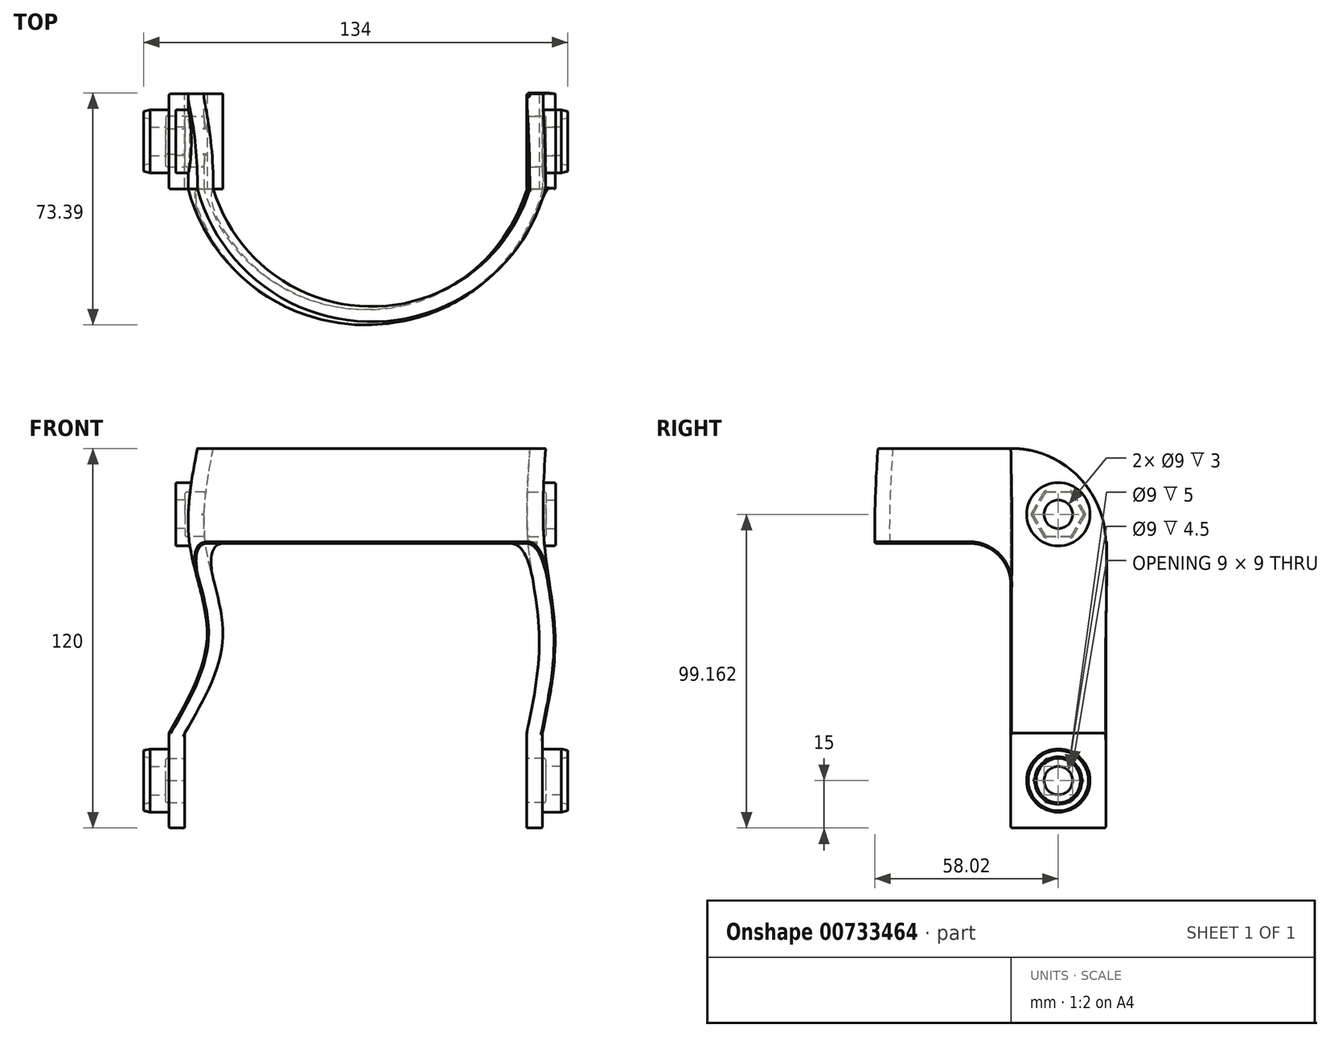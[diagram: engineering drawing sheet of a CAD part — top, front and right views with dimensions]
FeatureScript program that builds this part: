
annotation { "Feature Type Name" : "Feature", "Feature Type Description" : "" }
export const myFeature = defineFeature(function(context is Context, id is Id, definition is map)
    precondition{}
    {
        {
            var Q0;
            Q0=qCreatedBy(makeId("Top.planeOp"),FACE);
            cPlane(context, id + "F0", {"entities" : qUnion([Q0]), "cplaneType" : CPlaneType.OFFSET, "offset" : 30 * mm, "width" : 150 * mm, "height" : 150 * mm});
        }
        {
            var Q0;
            Q0=qCreatedBy(id+"F0.planeOp",FACE);
            var sketch = newSketch(context, id + "F1", { "sketchPlane" : qUnion([Q0])});
            skLineSegment(sketch, "E0", {"start": v(-54, 0) * mm, "end": v(-54, 15) * mm});
            skLineSegment(sketch, "E1", {"start": v(-54, 15) * mm, "end": v(-59, 15) * mm});
            skLineSegment(sketch, "E2", {"start": v(-59, 15) * mm, "end": v(-59, -15) * mm});
            skLineSegment(sketch, "E3", {"start": v(-54, -15) * mm, "end": v(-54, 0) * mm});
            skLineSegment(sketch, "E4", {"start": v(54, 0) * mm, "end": v(54, 15) * mm});
            skLineSegment(sketch, "E5", {"start": v(54, 15) * mm, "end": v(59, 15) * mm});
            skLineSegment(sketch, "E6", {"start": v(59, 15) * mm, "end": v(59, -15) * mm});
            skLineSegment(sketch, "E7", {"start": v(54, -15) * mm, "end": v(54, 0) * mm});
            skArc(sketch, "E8", {"start": v(-54, -15) * mm, "mid": v(0, -56.04) * mm, "end": v(54, -15) * mm});
            skArc(sketch, "E9", {"start": v(59, -15) * mm, "mid": v(0, -60.88) * mm, "end": v(-59, -15) * mm});
            skPoint(sketch, "E10", {"position": v(0, -56.04) * mm});
            skPoint(sketch, "E11", {"position": v(0, -60.88) * mm});
            skSolve(sketch);
        }
        {
            var Q0;
            Q0=qCreatedBy(makeId("Top.planeOp"),FACE);
            var sketch = newSketch(context, id + "F2", { "sketchPlane" : qUnion([Q0])});
            skLineSegment(sketch, "E12", {"start": v(-54, 0) * mm, "end": v(-54, 15) * mm});
            skLineSegment(sketch, "E13", {"start": v(-54, 15) * mm, "end": v(-59, 15) * mm});
            skLineSegment(sketch, "E14", {"start": v(-59, 15) * mm, "end": v(-59, -15) * mm});
            skLineSegment(sketch, "E15", {"start": v(-54, -15) * mm, "end": v(-54, 0) * mm});
            skLineSegment(sketch, "E16", {"start": v(54, 0) * mm, "end": v(54, 15) * mm});
            skLineSegment(sketch, "E17", {"start": v(54, 15) * mm, "end": v(59, 15) * mm});
            skLineSegment(sketch, "E18", {"start": v(59, 15) * mm, "end": v(59, -15) * mm});
            skLineSegment(sketch, "E19", {"start": v(54, -15) * mm, "end": v(54, 0) * mm});
            skArc(sketch, "E20", {"start": v(-54, -15) * mm, "mid": v(0, -56.04) * mm, "end": v(54, -15) * mm});
            skArc(sketch, "E21", {"start": v(59, -15) * mm, "mid": v(0, -60.88) * mm, "end": v(-59, -15) * mm});
            skPoint(sketch, "E22", {"position": v(0, -56.04) * mm});
            skPoint(sketch, "E23", {"position": v(0, -60.88) * mm});
            skSolve(sketch);
        }
        {
            var Q0;
            Q0=qCreatedBy(makeId("Top.planeOp"),FACE);
            cPlane(context, id + "F3", {"entities" : qUnion([Q0]), "cplaneType" : CPlaneType.OFFSET, "offset" : 60 * mm, "width" : 150 * mm, "height" : 150 * mm});
        }
        {
            var Q0;
            Q0=qCreatedBy(id+"F3.planeOp",FACE);
            var sketch = newSketch(context, id + "F4", { "sketchPlane" : qUnion([Q0])});
            skPoint(sketch, "E24", {"position": v(8, 0) * mm});
            skPoint(sketch, "E25", {"position": v(-42, 0) * mm});
            skPoint(sketch, "E26", {"position": v(58, 0) * mm});
            skLineSegment(sketch, "E27", {"start": v(-42, 0) * mm, "end": v(-42, -15) * mm});
            skLineSegment(sketch, "E28", {"start": v(-47, -15) * mm, "end": v(-47, 15) * mm});
            skLineSegment(sketch, "E29", {"start": v(-47, 15) * mm, "end": v(-42, 15) * mm});
            skLineSegment(sketch, "E30", {"start": v(-42, 15) * mm, "end": v(-42, 0) * mm});
            skLineSegment(sketch, "E31", {"start": v(58, 0) * mm, "end": v(58, 15) * mm});
            skLineSegment(sketch, "E32", {"start": v(58, 15) * mm, "end": v(63, 15) * mm});
            skLineSegment(sketch, "E33", {"start": v(63, 15) * mm, "end": v(63, -15) * mm});
            skLineSegment(sketch, "E34", {"start": v(58, -15) * mm, "end": v(58, 0) * mm});
            skArc(sketch, "E35", {"start": v(-42, -15) * mm, "mid": v(8, -52.2) * mm, "end": v(58, -15) * mm});
            skArc(sketch, "E36", {"start": v(-47, -15) * mm, "mid": v(8, -57) * mm, "end": v(63, -15) * mm});
            skSolve(sketch);
        }
        {
            var Q0;
            Q0=qCreatedBy(makeId("Top.planeOp"),FACE);
            cPlane(context, id + "F5", {"entities" : qUnion([Q0]), "cplaneType" : CPlaneType.OFFSET, "offset" : 90 * mm, "width" : 150 * mm, "height" : 150 * mm});
        }
        {
            var Q0;
            Q0=qCreatedBy(id+"F5.planeOp",FACE);
            var sketch = newSketch(context, id + "F6", { "sketchPlane" : qUnion([Q0])});
            skPoint(sketch, "E37", {"position": v(3.5, 0) * mm});
            skPoint(sketch, "E38", {"position": v(-47.5, 0) * mm});
            skPoint(sketch, "E39", {"position": v(54.5, 0) * mm});
            skLineSegment(sketch, "E40", {"start": v(-47.5, 0) * mm, "end": v(-47.5, 15) * mm});
            skLineSegment(sketch, "E41", {"start": v(-47.5, 15) * mm, "end": v(-52.5, 15) * mm});
            skLineSegment(sketch, "E42", {"start": v(-52.5, 15) * mm, "end": v(-52.5, -15) * mm});
            skLineSegment(sketch, "E43", {"start": v(-47.5, -15) * mm, "end": v(-47.5, 0) * mm});
            skLineSegment(sketch, "E44", {"start": v(54.5, 0) * mm, "end": v(54.5, 15.37) * mm});
            skLineSegment(sketch, "E45", {"start": v(54.5, 15.37) * mm, "end": v(59.6, 15.37) * mm});
            skLineSegment(sketch, "E46", {"start": v(59.6, 15.37) * mm, "end": v(59.6, -14.63) * mm});
            skLineSegment(sketch, "E47", {"start": v(54.5, -15) * mm, "end": v(54.5, 0) * mm});
            skArc(sketch, "E48", {"start": v(-47.5, -15) * mm, "mid": v(3.5, -53.16) * mm, "end": v(54.5, -15) * mm});
            skArc(sketch, "E49", {"start": v(-52.5, -15) * mm, "mid": v(3.69, -57.97) * mm, "end": v(59.6, -14.63) * mm});
            skSolve(sketch);
        }
        {
            var Q0;
            Q0=qCreatedBy(makeId("Top.planeOp"),FACE);
            cPlane(context, id + "F7", {"entities" : qUnion([Q0]), "cplaneType" : CPlaneType.OFFSET, "offset" : 120 * mm, "width" : 150 * mm, "height" : 150 * mm});
        }
        {
            var Q0;
            Q0=qCreatedBy(id+"F7.planeOp",FACE);
            var sketch = newSketch(context, id + "F8", { "sketchPlane" : qUnion([Q0])});
            skPoint(sketch, "E50", {"position": v(5, 0) * mm});
            skPoint(sketch, "E51", {"position": v(-45, 0) * mm});
            skPoint(sketch, "E52", {"position": v(55, 0) * mm});
            skLineSegment(sketch, "E53", {"start": v(-45, 0) * mm, "end": v(-45, 15) * mm});
            skLineSegment(sketch, "E54", {"start": v(-45, 15) * mm, "end": v(-50, 15) * mm});
            skLineSegment(sketch, "E55", {"start": v(-50, 15) * mm, "end": v(-50, -15) * mm});
            skLineSegment(sketch, "E56", {"start": v(-45, -15) * mm, "end": v(-45, 0) * mm});
            skLineSegment(sketch, "E57", {"start": v(55, 0) * mm, "end": v(55, -15) * mm});
            skLineSegment(sketch, "E58", {"start": v(60, -15) * mm, "end": v(60, 15) * mm});
            skLineSegment(sketch, "E59", {"start": v(60, 15) * mm, "end": v(55, 15) * mm});
            skLineSegment(sketch, "E60", {"start": v(55, 15) * mm, "end": v(55, 0) * mm});
            skArc(sketch, "E61", {"start": v(-45, -15) * mm, "mid": v(5, -52.2) * mm, "end": v(55, -15) * mm});
            skArc(sketch, "E62", {"start": v(-50, -15) * mm, "mid": v(5, -57) * mm, "end": v(60, -15) * mm});
            skSolve(sketch);
        }
        {
            var Q0;
            Q0=makeQuery(id+"F1.imprint","IMPRINT",FACE,{"disambiguationData":[TD([[makeQuery(id+"F1.imprint","IMPRINT",EDGE,{"derivedFrom":sQuery(id+"F1.wireOp",EDGE,"E0")}),1.0]])]});
            var Q1;
            Q1=makeQuery(id+"F4.imprint","IMPRINT",FACE,{"disambiguationData":[TD([[makeQuery(id+"F4.imprint","IMPRINT",EDGE,{"derivedFrom":sQuery(id+"F4.wireOp",EDGE,"E27")}),-1.0]])]});
            var Q2;
            Q2=makeQuery(id+"F6.imprint","IMPRINT",FACE,{"disambiguationData":[TD([[makeQuery(id+"F6.imprint","IMPRINT",EDGE,{"derivedFrom":sQuery(id+"F6.wireOp",EDGE,"E40")}),1.0]])]});
            var Q3;
            Q3=makeQuery(id+"F8.imprint","IMPRINT",FACE,{"disambiguationData":[TD([[makeQuery(id+"F8.imprint","IMPRINT",EDGE,{"derivedFrom":sQuery(id+"F8.wireOp",EDGE,"E53")}),1.0]])]});
            loft(context, id + "F9", {"sheetProfilesArray" : [{ "sheetProfileEntities" : qUnion([Q0]) }, { "sheetProfileEntities" : qUnion([Q1]) }, { "sheetProfileEntities" : qUnion([Q2]) }, { "sheetProfileEntities" : qUnion([Q3]) }]});
        }
        {
            var Q0;
            Q0=makeQuery(id+"F2.imprint","IMPRINT",FACE,{"disambiguationData":[TD([[makeQuery(id+"F2.imprint","IMPRINT",EDGE,{"derivedFrom":sQuery(id+"F2.wireOp",EDGE,"E12")}),1.0]])]});
            extrude(context, id + "F10", {"entities" : qUnion([Q0]), "operationType" : NewBodyOperationType.ADD, "depth" : 30 * mm, "offsetDistance" : 25 * mm});
        }
        {
            var Q0;
            Q0=qCreatedBy(makeId("Right.planeOp"),FACE);
            var sketch = newSketch(context, id + "F11", { "sketchPlane" : qUnion([Q0])});
            skPoint(sketch, "E63", {"position": v(82.65, 59.89) * mm});
            skPoint(sketch, "E64", {"position": v(-15, 120) * mm});
            skPoint(sketch, "E65", {"position": v(-15, 90) * mm});
            skArc(sketch, "E66", {"start": v(-15, 120) * mm, "mid": v(6.21, 111.21) * mm, "end": v(15, 90) * mm});
            skPoint(sketch, "E67", {"position": v(-28.01, 76.99) * mm});
            skArc(sketch, "E68", {"start": v(-15, 76.99) * mm, "mid": v(-18.81, 86.19) * mm, "end": v(-28.01, 90) * mm});
            skLineSegment(sketch, "E69", {"start": v(-15, 76.99) * mm, "end": v(-15, -61.51) * mm});
            skLineSegment(sketch, "E70", {"start": v(-15, -61.51) * mm, "end": v(-141.22, -61.51) * mm});
            skLineSegment(sketch, "E71", {"start": v(-141.22, -61.51) * mm, "end": v(-141.22, 174.74) * mm});
            skLineSegment(sketch, "E72", {"start": v(-141.22, 174.74) * mm, "end": v(85.32, 174.74) * mm});
            skLineSegment(sketch, "E73", {"start": v(85.32, 174.74) * mm, "end": v(15, 90) * mm});
            skLineSegment(sketch, "E74", {"start": v(-28.01, 90) * mm, "end": v(-81.35, 90) * mm});
            skLineSegment(sketch, "E75", {"start": v(-81.35, 90) * mm, "end": v(-81.35, 120) * mm});
            skLineSegment(sketch, "E76", {"start": v(-81.35, 120) * mm, "end": v(-15, 120) * mm});
            skSolve(sketch);
        }
        {
            var Q0;
            Q0=qSketchRegion(id+"F11",true);
            extrude(context, id + "F12", {"entities" : qUnion([Q0]), "operationType" : NewBodyOperationType.REMOVE, "oppositeDirection" : true, "depth" : 100 * mm, "offsetDistance" : 25 * mm, "hasSecondDirection" : true, "secondDirectionOppositeDirection" : false, "secondDirectionDepth" : 100 * mm});
        }
        {
            var Q0;
            Q0=makeQuery(id+"F10.opExtrude","SWEPT_FACE",FACE,{"disambiguationData":[OSD([sQuery(id+"F2.wireOp",EDGE,"E14")])]});
            var sketch = newSketch(context, id + "F13", { "sketchPlane" : qUnion([Q0])});
            skPoint(sketch, "E77", {"position": v(0, 15) * mm});
            skCircle(sketch, "E78", {"center": v(0, 15) * mm, "radius": 10 * mm});
            skSolve(sketch);
        }
        {
            var Q0;
            Q0=makeQuery(id+"F13.imprint","IMPRINT",FACE,{"disambiguationData":[TD([[makeQuery(id+"F13.imprint","IMPRINT",EDGE,{"derivedFrom":sQuery(id+"F13.wireOp",EDGE,"E78")}),1.0]])]});
            extrude(context, id + "F14", {"entities" : qUnion([Q0]), "operationType" : NewBodyOperationType.ADD, "depth" : 6 * mm, "offsetDistance" : 25 * mm});
        }
        {
            var Q0;
            Q0=qCreatedBy(makeId("Front.planeOp"),FACE);
            var sketch = newSketch(context, id + "F15", { "sketchPlane" : qUnion([Q0])});
            skPoint(sketch, "E79", {"position": v(-54, 15) * mm});
            skPoint(sketch, "E80", {"position": v(-49.01, 23.39) * mm});
            skPoint(sketch, "E81", {"position": v(-65, 15) * mm});
            skLineSegment(sketch, "E82", {"start": v(-65, 22) * mm, "end": v(-65, 25) * mm});
            skLineSegment(sketch, "E83", {"start": v(-65, 25) * mm, "end": v(-67, 24.5) * mm});
            skLineSegment(sketch, "E84", {"start": v(-67, 24.5) * mm, "end": v(-67, 22.5) * mm});
            skLineSegment(sketch, "E85", {"start": v(-67, 22.5) * mm, "end": v(-65, 22) * mm});
            skPoint(sketch, "E86", {"position": v(-65, 23.5) * mm});
            skPoint(sketch, "E87", {"position": v(-67, 23.5) * mm});
            skLineSegment(sketch, "E88", {"start": v(-65, 15) * mm, "end": v(-67, 15) * mm});
            skLineSegment(sketch, "E89", {"start": v(-65, 22) * mm, "end": v(-67, 22.5) * mm});
            skLineSegment(sketch, "E90", {"start": v(-67, 22.5) * mm, "end": v(-67, 24.5) * mm});
            skLineSegment(sketch, "E91", {"start": v(-67, 24.5) * mm, "end": v(-65, 25) * mm});
            skLineSegment(sketch, "E92", {"start": v(-65, 25) * mm, "end": v(-65, 22) * mm});
            skSolve(sketch);
        }
        {
            var Q0;
            Q0 = qSketchRegion(id + "F15", true);
            var Q1;
            Q1=sQuery(id+"F15.wireOp",EDGE,"E88");
            revolve(context, id + "F16", {"operationType" : NewBodyOperationType.ADD, "surfaceOperationType" : NewSurfaceOperationType.NEW, "entities" : qUnion([Q0]), "axis" : qUnion([Q1]), "revolveType" : RevolveType.FULL});
        }
        {
            var Q0;
            Q0=makeQuery(id+"F10.opExtrude","SWEPT_FACE",FACE,{"disambiguationData":[OSD([sQuery(id+"F2.wireOp",EDGE,"E12"),sQuery(id+"F2.wireOp",EDGE,"E15")])]});
            var sketch = newSketch(context, id + "F17", { "sketchPlane" : qUnion([Q0])});
            skPoint(sketch, "E93", {"position": v(0, 15) * mm});
            skCircle(sketch, "E94", {"center": v(0, 15) * mm, "radius": 4.5 * mm});
            skSolve(sketch);
        }
        {
            var Q0;
            Q0 = qSketchRegion(id + "F17", true);
            extrude(context, id + "F18", {"entities" : qUnion([Q0]), "operationType" : NewBodyOperationType.REMOVE, "oppositeDirection" : true, "depth" : 25 * mm, "offsetDistance" : 25 * mm});
        }
        {
            var Q0;
            Q0=makeQuery(id+"F10.opExtrude","SWEPT_FACE",FACE,{"disambiguationData":[OSD([sQuery(id+"F2.wireOp",EDGE,"E12"),sQuery(id+"F2.wireOp",EDGE,"E15")])]});
            var sketch = newSketch(context, id + "F19", { "sketchPlane" : qUnion([Q0])});
            skPoint(sketch, "E95", {"position": v(0, 15) * mm});
            skCircle(sketch, "E96", {"center": v(0, 15) * mm, "radius": 4.5 * mm});
            skSolve(sketch);
        }
        {
            var Q0;
            Q0=makeQuery(id+"F19.imprint","IMPRINT",FACE,{"disambiguationData":[TD([[makeQuery(id+"F19.imprint","IMPRINT",EDGE,{"derivedFrom":sQuery(id+"F19.wireOp",EDGE,"E96")}),-1.0]])]});
            var sketch = newSketch(context, id + "F20", { "sketchPlane" : qUnion([Q0])});
            skPoint(sketch, "E97", {"position": v(0, 15) * mm});
            skCircle(sketch, "E98", {"center": v(0, 15) * mm, "radius": 7 * mm});
            skPoint(sketch, "E99", {"position": v(0, 22) * mm});
            skCircle(sketch, "E100.cCircle", {"center": v(0, 15) * mm, "radius": 7 * mm, "construction": true});
            skLineSegment(sketch, "E100.0", {"start": v(-4.04, 22) * mm, "end": v(4.04, 22) * mm});
            skLineSegment(sketch, "E100.1", {"start": v(4.04, 22) * mm, "end": v(8.08, 15) * mm});
            skLineSegment(sketch, "E100.2", {"start": v(8.08, 15) * mm, "end": v(4.04, 8) * mm});
            skLineSegment(sketch, "E100.3", {"start": v(4.04, 8) * mm, "end": v(-4.04, 8) * mm});
            skLineSegment(sketch, "E100.4", {"start": v(-4.04, 8) * mm, "end": v(-8.08, 15) * mm});
            skLineSegment(sketch, "E100.5", {"start": v(-8.08, 15) * mm, "end": v(-4.04, 22) * mm});
            skSolve(sketch);
        }
        {
            var Q0;
            Q0 = qSketchRegion(id + "F20", true);
            extrude(context, id + "F21", {"entities" : qUnion([Q0]), "operationType" : NewBodyOperationType.REMOVE, "oppositeDirection" : true, "depth" : 6 * mm, "offsetDistance" : 25 * mm});
        }
        {
            var Q0;
            Q0=makeQuery(id+"F10.opExtrude","SWEPT_FACE",FACE,{"disambiguationData":[OSD([sQuery(id+"F2.wireOp",EDGE,"E18")])]});
            var sketch = newSketch(context, id + "F22", { "sketchPlane" : qUnion([Q0])});
            skPoint(sketch, "E101", {"position": v(0, 15) * mm});
            skCircle(sketch, "E102", {"center": v(0, 15) * mm, "radius": 10 * mm});
            skSolve(sketch);
        }
        {
            var Q0;
            Q0 = qSketchRegion(id + "F22", true);
            extrude(context, id + "F23", {"entities" : qUnion([Q0]), "operationType" : NewBodyOperationType.ADD, "depth" : 6 * mm, "offsetDistance" : 25 * mm});
        }
        {
            var Q0;
            Q0=qCreatedBy(makeId("Front.planeOp"),FACE);
            var sketch = newSketch(context, id + "F24", { "sketchPlane" : qUnion([Q0])});
            skPoint(sketch, "E103", {"position": v(54, 15) * mm});
            skPoint(sketch, "E104", {"position": v(32.82, 5.22) * mm});
            skPoint(sketch, "E105", {"position": v(65, 15) * mm});
            skLineSegment(sketch, "E106", {"start": v(65, 8) * mm, "end": v(65, 5) * mm});
            skLineSegment(sketch, "E107", {"start": v(65, 5) * mm, "end": v(67, 5.5) * mm});
            skLineSegment(sketch, "E108", {"start": v(67, 5.5) * mm, "end": v(67, 7.5) * mm});
            skLineSegment(sketch, "E109", {"start": v(67, 7.5) * mm, "end": v(65, 8) * mm});
            skPoint(sketch, "E110", {"position": v(65, 6.5) * mm});
            skPoint(sketch, "E111", {"position": v(67, 6.5) * mm});
            skLineSegment(sketch, "E112", {"start": v(65, 15) * mm, "end": v(67, 15) * mm});
            skLineSegment(sketch, "E113", {"start": v(65, 8) * mm, "end": v(67, 7.5) * mm});
            skLineSegment(sketch, "E114", {"start": v(67, 7.5) * mm, "end": v(67, 5.5) * mm});
            skLineSegment(sketch, "E115", {"start": v(67, 5.5) * mm, "end": v(65, 5) * mm});
            skLineSegment(sketch, "E116", {"start": v(65, 5) * mm, "end": v(65, 8) * mm});
            skSolve(sketch);
        }
        {
            var Q0;
            Q0 = qSketchRegion(id + "F24", true);
            var Q1;
            Q1=sQuery(id+"F24.wireOp",EDGE,"E112");
            revolve(context, id + "F25", {"operationType" : NewBodyOperationType.ADD, "surfaceOperationType" : NewSurfaceOperationType.NEW, "entities" : qUnion([Q0]), "axis" : qUnion([Q1]), "revolveType" : RevolveType.FULL});
        }
        {
            var Q0;
            Q0=makeQuery(id+"F10.opExtrude","SWEPT_FACE",FACE,{"disambiguationData":[OSD([sQuery(id+"F2.wireOp",EDGE,"E16"),sQuery(id+"F2.wireOp",EDGE,"E19")])]});
            var sketch = newSketch(context, id + "F26", { "sketchPlane" : qUnion([Q0])});
            skPoint(sketch, "E117", {"position": v(0, 15) * mm});
            skCircle(sketch, "E118", {"center": v(0, 15) * mm, "radius": 4.5 * mm});
            skSolve(sketch);
        }
        {
            var Q0;
            Q0 = qSketchRegion(id + "F26", true);
            extrude(context, id + "F27", {"entities" : qUnion([Q0]), "operationType" : NewBodyOperationType.REMOVE, "oppositeDirection" : true, "depth" : 25 * mm, "offsetDistance" : 25 * mm});
        }
        {
            var Q0;
            Q0=makeQuery(id+"F10.opExtrude","SWEPT_FACE",FACE,{"disambiguationData":[OSD([sQuery(id+"F2.wireOp",EDGE,"E16"),sQuery(id+"F2.wireOp",EDGE,"E19")])]});
            var sketch = newSketch(context, id + "F28", { "sketchPlane" : qUnion([Q0])});
            skPoint(sketch, "E119", {"position": v(0, 15) * mm});
            skCircle(sketch, "E120", {"center": v(0, 15) * mm, "radius": 7 * mm});
            skPoint(sketch, "E121", {"position": v(0, 22) * mm});
            skCircle(sketch, "E122.cCircle", {"center": v(0, 15) * mm, "radius": 7 * mm, "construction": true});
            skLineSegment(sketch, "E122.0", {"start": v(-4.04, 22) * mm, "end": v(4.04, 22) * mm});
            skLineSegment(sketch, "E122.1", {"start": v(4.04, 22) * mm, "end": v(8.08, 15) * mm});
            skLineSegment(sketch, "E122.2", {"start": v(8.08, 15) * mm, "end": v(4.04, 8) * mm});
            skLineSegment(sketch, "E122.3", {"start": v(4.04, 8) * mm, "end": v(-4.04, 8) * mm});
            skLineSegment(sketch, "E122.4", {"start": v(-4.04, 8) * mm, "end": v(-8.08, 15) * mm});
            skLineSegment(sketch, "E122.5", {"start": v(-8.08, 15) * mm, "end": v(-4.04, 22) * mm});
            skSolve(sketch);
        }
        {
            var Q0;
            Q0 = qSketchRegion(id + "F28", true);
            extrude(context, id + "F29", {"entities" : qUnion([Q0]), "operationType" : NewBodyOperationType.REMOVE, "oppositeDirection" : true, "depth" : 6 * mm, "offsetDistance" : 25 * mm});
        }
        {
            var Q0;
            Q0=qCreatedBy(makeId("Right.planeOp"),FACE);
            cPlane(context, id + "F30", {"entities" : qUnion([Q0]), "cplaneType" : CPlaneType.OFFSET, "offset" : 57.3 * mm, "oppositeDirection" : true, "width" : 150 * mm, "height" : 150 * mm});
        }
        {
            var Q0;
            Q0=qCreatedBy(makeId("Front.planeOp"),FACE);
            var sketch = newSketch(context, id + "F31", { "sketchPlane" : qUnion([Q0])});
            skPoint(sketch, "E123", {"position": v(-47.9, 99.16) * mm});
            skPoint(sketch, "E124", {"position": v(-56.9, 99.16) * mm});
            skPoint(sketch, "E125", {"position": v(-57.3, 99.16) * mm});
            skSolve(sketch);
        }
        {
            var Q0;
            Q0=qCreatedBy(id+"F30.planeOp",FACE);
            cPlane(context, id + "F32", {"entities" : qUnion([Q0]), "cplaneType" : CPlaneType.OFFSET, "offset" : 0.4 * mm, "width" : 150 * mm, "height" : 150 * mm});
        }
        {
            var Q0;
            Q0=qCreatedBy(id+"F32.planeOp",FACE);
            var sketch = newSketch(context, id + "F33", { "sketchPlane" : qUnion([Q0])});
            skPoint(sketch, "E126", {"position": v(0, 99.16) * mm});
            skCircle(sketch, "E127", {"center": v(0, 99.16) * mm, "radius": 10 * mm});
            skSolve(sketch);
        }
        {
            var Q0;
            Q0 = qSketchRegion(id + "F33", true);
            extrude(context, id + "F34", {"entities" : qUnion([Q0]), "operationType" : NewBodyOperationType.ADD, "depth" : 5 * mm, "offsetDistance" : 25 * mm});
        }
        {
            var Q0;
            Q0=makeQuery(id+"F34.opExtrude","CAP_FACE",FACE,{"disambiguationData":[OSD([sQuery(id+"F33.wireOp",EDGE,"E127")])],"isStart":true});
            var sketch = newSketch(context, id + "F35", { "sketchPlane" : qUnion([Q0])});
            skCircle(sketch, "E128", {"center": v(0, 99.16) * mm, "radius": 4.5 * mm});
            skSolve(sketch);
        }
        {
            var Q0;
            Q0 = qSketchRegion(id + "F35", true);
            extrude(context, id + "F36", {"entities" : qUnion([Q0]), "operationType" : NewBodyOperationType.REMOVE, "oppositeDirection" : true, "depth" : 25 * mm, "offsetDistance" : 25 * mm});
        }
        {
            var Q0;
            Q0=makeQuery(id+"F34.opExtrude","CAP_FACE",FACE,{"disambiguationData":[OSD([sQuery(id+"F33.wireOp",EDGE,"E127")])],"isStart":true});
            var sketch = newSketch(context, id + "F37", { "sketchPlane" : qUnion([Q0])});
            skPoint(sketch, "E129", {"position": v(-6.55, 97.38) * mm});
            skPoint(sketch, "E130", {"position": v(0, 99.16) * mm});
            skCircle(sketch, "E131", {"center": v(0, 99.16) * mm, "radius": 7 * mm});
            skPoint(sketch, "E132", {"position": v(0, 106.16) * mm});
            skCircle(sketch, "E133.cCircle", {"center": v(0, 99.16) * mm, "radius": 7 * mm, "construction": true});
            skLineSegment(sketch, "E133.0", {"start": v(-4.04, 106.16) * mm, "end": v(4.04, 106.16) * mm});
            skLineSegment(sketch, "E133.1", {"start": v(4.04, 106.16) * mm, "end": v(8.08, 99.16) * mm});
            skLineSegment(sketch, "E133.2", {"start": v(8.08, 99.16) * mm, "end": v(4.04, 92.16) * mm});
            skLineSegment(sketch, "E133.3", {"start": v(4.04, 92.16) * mm, "end": v(-4.04, 92.16) * mm});
            skLineSegment(sketch, "E133.4", {"start": v(-4.04, 92.16) * mm, "end": v(-8.08, 99.16) * mm});
            skLineSegment(sketch, "E133.5", {"start": v(-8.08, 99.16) * mm, "end": v(-4.04, 106.16) * mm});
            skSolve(sketch);
        }
        {
            var Q0;
            Q0 = qSketchRegion(id + "F37", true);
            extrude(context, id + "F38", {"entities" : qUnion([Q0]), "operationType" : NewBodyOperationType.REMOVE, "oppositeDirection" : true, "depth" : 25 * mm, "offsetDistance" : 25 * mm, "hasSecondDirection" : true, "secondDirectionOppositeDirection" : true, "secondDirectionDepth" : 3 * mm});
        }
        {
            var Q0;
            Q0=qCreatedBy(makeId("Right.planeOp"),FACE);
            cPlane(context, id + "F39", {"entities" : qUnion([Q0]), "cplaneType" : CPlaneType.OFFSET, "offset" : 67 * mm, "width" : 150 * mm, "height" : 150 * mm});
        }
        {
            var Q0;
            Q0=qCreatedBy(id+"F39.planeOp",FACE);
            cPlane(context, id + "F40", {"entities" : qUnion([Q0]), "cplaneType" : CPlaneType.OFFSET, "offset" : 3.84 * mm, "oppositeDirection" : true, "width" : 150 * mm, "height" : 150 * mm});
        }
        {
            var Q0;
            Q0=qCreatedBy(id+"F40.planeOp",FACE);
            var sketch = newSketch(context, id + "F41", { "sketchPlane" : qUnion([Q0])});
            skPoint(sketch, "E134", {"position": v(0, 99.16) * mm});
            skCircle(sketch, "E135", {"center": v(0, 99.16) * mm, "radius": 10 * mm});
            skSolve(sketch);
        }
        {
            var Q0;
            Q0 = qSketchRegion(id + "F41", true);
            extrude(context, id + "F42", {"entities" : qUnion([Q0]), "operationType" : NewBodyOperationType.ADD, "oppositeDirection" : true, "depth" : 5 * mm, "offsetDistance" : 25 * mm});
        }
        {
            var Q0;
            Q0=makeQuery(id+"F42.opExtrude","CAP_FACE",FACE,{"disambiguationData":[OSD([sQuery(id+"F41.wireOp",EDGE,"E135")])],"isStart":true});
            var sketch = newSketch(context, id + "F43", { "sketchPlane" : qUnion([Q0])});
            skPoint(sketch, "E136", {"position": v(0, 99.16) * mm});
            skCircle(sketch, "E137", {"center": v(0, 99.16) * mm, "radius": 4.5 * mm});
            skSolve(sketch);
        }
        {
            var Q0;
            Q0 = qSketchRegion(id + "F43", true);
            extrude(context, id + "F44", {"entities" : qUnion([Q0]), "operationType" : NewBodyOperationType.REMOVE, "oppositeDirection" : true, "depth" : 25 * mm, "offsetDistance" : 25 * mm});
        }
        {
            var Q0;
            Q0=makeQuery(id+"F42.opExtrude","CAP_FACE",FACE,{"disambiguationData":[OSD([sQuery(id+"F41.wireOp",EDGE,"E135")])],"isStart":true});
            var sketch = newSketch(context, id + "F45", { "sketchPlane" : qUnion([Q0])});
            skPoint(sketch, "E138", {"position": v(-0.57, 99.82) * mm});
            skPoint(sketch, "E139", {"position": v(0, 99.16) * mm});
            skCircle(sketch, "E140", {"center": v(0, 99.16) * mm, "radius": 7 * mm});
            skPoint(sketch, "E141", {"position": v(0, 106.16) * mm});
            skCircle(sketch, "E142.cCircle", {"center": v(0, 99.16) * mm, "radius": 7 * mm, "construction": true});
            skLineSegment(sketch, "E142.0", {"start": v(-4.04, 106.16) * mm, "end": v(4.04, 106.16) * mm});
            skLineSegment(sketch, "E142.1", {"start": v(4.04, 106.16) * mm, "end": v(8.08, 99.16) * mm});
            skLineSegment(sketch, "E142.2", {"start": v(8.08, 99.16) * mm, "end": v(4.04, 92.16) * mm});
            skLineSegment(sketch, "E142.3", {"start": v(4.04, 92.16) * mm, "end": v(-4.04, 92.16) * mm});
            skLineSegment(sketch, "E142.4", {"start": v(-4.04, 92.16) * mm, "end": v(-8.08, 99.16) * mm});
            skLineSegment(sketch, "E142.5", {"start": v(-8.08, 99.16) * mm, "end": v(-4.04, 106.16) * mm});
            skSolve(sketch);
        }
        {
            var Q0;
            Q0 = qSketchRegion(id + "F45", true);
            extrude(context, id + "F46", {"entities" : qUnion([Q0]), "operationType" : NewBodyOperationType.REMOVE, "oppositeDirection" : true, "depth" : 25 * mm, "offsetDistance" : 25 * mm, "hasSecondDirection" : true, "secondDirectionOppositeDirection" : true, "secondDirectionDepth" : 3 * mm});
        }
        {
            var Q0;
            Q0=makeQuery(id+"F12.boolean.opBoolean","INTERSECT",EDGE,{"derivedFrom":[makeQuery(id+"F9.opLoft","SWEPT_FACE",FACE,{"disambiguationData":[OSD([sQuery(id+"F1.wireOp",EDGE,"E2"),sQuery(id+"F1.wireOp",EDGE,"E6"),sQuery(id+"F1.wireOp",EDGE,"E9"),sQuery(id+"F4.wireOp",EDGE,"E28"),sQuery(id+"F4.wireOp",EDGE,"E33"),sQuery(id+"F4.wireOp",EDGE,"E36")])]}),makeQuery(id+"F12.opExtrude","SWEPT_FACE",FACE,{"disambiguationData":[OSD([sQuery(id+"F11.wireOp",EDGE,"E74")])]})]});
            var Q1;
            Q1=makeQuery(id+"F10.opExtrude","CAP_EDGE",EDGE,{"disambiguationData":[OSD([sQuery(id+"F2.wireOp",EDGE,"E14")])],"isStart":true});
            var Q2;
            Q2=makeQuery(id+"F10.opExtrude","SWEPT_EDGE",EDGE,{"disambiguationData":[OSD([sQuery(id+"F2.wireOp",EDGE,"E14"),sQuery(id+"F2.wireOp",EDGE,"E21")])]});
            var Q3;
            Q3=makeQuery(id+"F10.opExtrude","SWEPT_EDGE",EDGE,{"disambiguationData":[OSD([sQuery(id+"F2.wireOp",EDGE,"E13"),sQuery(id+"F2.wireOp",EDGE,"E14")])]});
            var Q4;
            Q4=makeQuery(id+"F10.opExtrude","CAP_EDGE",EDGE,{"disambiguationData":[OSD([sQuery(id+"F2.wireOp",EDGE,"E13")])],"isStart":true});
            var Q5;
            Q5=makeQuery(id+"F12.boolean.opBoolean","INTERSECT",EDGE,{"disambiguationData":[OD(0.0)],"derivedFrom":[makeQuery(id+"F10.opExtrude","CAP_FACE",FACE,{"disambiguationData":[OSD([sQuery(id+"F2.wireOp",EDGE,"E12"),sQuery(id+"F2.wireOp",EDGE,"E13"),sQuery(id+"F2.wireOp",EDGE,"E14"),sQuery(id+"F2.wireOp",EDGE,"E15"),sQuery(id+"F2.wireOp",EDGE,"E16"),sQuery(id+"F2.wireOp",EDGE,"E17"),sQuery(id+"F2.wireOp",EDGE,"E18"),sQuery(id+"F2.wireOp",EDGE,"E19"),sQuery(id+"F2.wireOp",EDGE,"E20"),sQuery(id+"F2.wireOp",EDGE,"E21")])],"isStart":true}),makeQuery(id+"F12.opExtrude","SWEPT_FACE",FACE,{"disambiguationData":[OSD([sQuery(id+"F11.wireOp",EDGE,"E69")])]})]});
            var Q6;
            Q6=makeQuery(id+"F10.opExtrude","CAP_EDGE",EDGE,{"disambiguationData":[OSD([sQuery(id+"F2.wireOp",EDGE,"E12"),sQuery(id+"F2.wireOp",EDGE,"E15")])],"isStart":true});
            var Q7;
            Q7=makeQuery(id+"F10.opExtrude","SWEPT_EDGE",EDGE,{"disambiguationData":[OSD([sQuery(id+"F2.wireOp",EDGE,"E12"),sQuery(id+"F2.wireOp",EDGE,"E13")])]});
            var Q8;
            Q8=makeQuery(id+"F10.opExtrude","SWEPT_EDGE",EDGE,{"disambiguationData":[OSD([sQuery(id+"F2.wireOp",EDGE,"E15"),sQuery(id+"F2.wireOp",EDGE,"E20")])]});
            var Q9;
            Q9=makeQuery(id+"F21.boolean.opBoolean","COPY",EDGE,{"derivedFrom":makeQuery(id+"F21.opExtrude","CAP_EDGE",EDGE,{"disambiguationData":[OSD([sQuery(id+"F20.wireOp",EDGE,"E100.1")])],"isStart":true})});
            var Q10;
            Q10=makeQuery(id+"F21.boolean.opBoolean","COPY",EDGE,{"derivedFrom":makeQuery(id+"F21.opExtrude","CAP_EDGE",EDGE,{"disambiguationData":[OSD([sQuery(id+"F20.wireOp",EDGE,"E100.0")])],"isStart":true})});
            var Q11;
            Q11=makeQuery(id+"F21.boolean.opBoolean","COPY",EDGE,{"derivedFrom":makeQuery(id+"F21.opExtrude","CAP_EDGE",EDGE,{"disambiguationData":[OSD([sQuery(id+"F20.wireOp",EDGE,"E100.5")])],"isStart":true})});
            var Q12;
            Q12=makeQuery(id+"F21.boolean.opBoolean","COPY",EDGE,{"derivedFrom":makeQuery(id+"F21.opExtrude","CAP_EDGE",EDGE,{"disambiguationData":[OSD([sQuery(id+"F20.wireOp",EDGE,"E100.4")])],"isStart":true})});
            var Q13;
            Q13=makeQuery(id+"F21.boolean.opBoolean","COPY",EDGE,{"derivedFrom":makeQuery(id+"F21.opExtrude","CAP_EDGE",EDGE,{"disambiguationData":[OSD([sQuery(id+"F20.wireOp",EDGE,"E100.3")])],"isStart":true})});
            var Q14;
            Q14=makeQuery(id+"F21.boolean.opBoolean","COPY",EDGE,{"derivedFrom":makeQuery(id+"F21.opExtrude","CAP_EDGE",EDGE,{"disambiguationData":[OSD([sQuery(id+"F20.wireOp",EDGE,"E100.2")])],"isStart":true})});
            var Q15;
            Q15=makeQuery(id+"F21.boolean.opBoolean","COPY",FACE,{"derivedFrom":makeQuery(id+"F21.opExtrude","CAP_FACE",FACE,{"disambiguationData":[OSD([sQuery(id+"F20.wireOp",EDGE,"E100.0"),sQuery(id+"F20.wireOp",EDGE,"E100.1"),sQuery(id+"F20.wireOp",EDGE,"E100.2"),sQuery(id+"F20.wireOp",EDGE,"E100.3"),sQuery(id+"F20.wireOp",EDGE,"E100.4"),sQuery(id+"F20.wireOp",EDGE,"E100.5")])],"isStart":false})});
            fillet(context, id + "F47", {"entities" : qUnion([Q0, Q1, Q2, Q3, Q4, Q5, Q6, Q7, Q8, Q9, Q10, Q11, Q12, Q13, Q14, Q15]), "radius" : 0.5 * mm, "tangentPropagation" : true, "allowEdgeOverflow" : false});
        }
        {
            var Q0;
            Q0=makeQuery(id+"F29.boolean.opBoolean","COPY",FACE,{"derivedFrom":makeQuery(id+"F29.opExtrude","SWEPT_FACE",FACE,{"disambiguationData":[OSD([sQuery(id+"F28.wireOp",EDGE,"E122.4")])]})});
            var Q1;
            Q1=makeQuery(id+"F29.boolean.opBoolean","COPY",FACE,{"derivedFrom":makeQuery(id+"F29.opExtrude","SWEPT_FACE",FACE,{"disambiguationData":[OSD([sQuery(id+"F28.wireOp",EDGE,"E122.5")])]})});
            var Q2;
            Q2=makeQuery(id+"F29.boolean.opBoolean","COPY",FACE,{"derivedFrom":makeQuery(id+"F29.opExtrude","SWEPT_FACE",FACE,{"disambiguationData":[OSD([sQuery(id+"F28.wireOp",EDGE,"E122.0")])]})});
            var Q3;
            Q3=makeQuery(id+"F29.boolean.opBoolean","COPY",FACE,{"derivedFrom":makeQuery(id+"F29.opExtrude","SWEPT_FACE",FACE,{"disambiguationData":[OSD([sQuery(id+"F28.wireOp",EDGE,"E122.1")])]})});
            var Q4;
            Q4=makeQuery(id+"F29.boolean.opBoolean","COPY",FACE,{"derivedFrom":makeQuery(id+"F29.opExtrude","SWEPT_FACE",FACE,{"disambiguationData":[OSD([sQuery(id+"F28.wireOp",EDGE,"E122.3")])]})});
            var Q5;
            Q5=makeQuery(id+"F29.boolean.opBoolean","COPY",FACE,{"derivedFrom":makeQuery(id+"F29.opExtrude","SWEPT_FACE",FACE,{"disambiguationData":[OSD([sQuery(id+"F28.wireOp",EDGE,"E122.2")])]})});
            var Q6;
            Q6=makeQuery(id+"F10.opExtrude","SWEPT_EDGE",EDGE,{"disambiguationData":[OSD([sQuery(id+"F2.wireOp",EDGE,"E18"),sQuery(id+"F2.wireOp",EDGE,"E21")])]});
            var Q7;
            Q7=makeQuery(id+"F10.opExtrude","SWEPT_EDGE",EDGE,{"disambiguationData":[OSD([sQuery(id+"F2.wireOp",EDGE,"E19"),sQuery(id+"F2.wireOp",EDGE,"E20")])]});
            var Q8;
            Q8=makeQuery(id+"F12.boolean.opBoolean","INTERSECT",EDGE,{"disambiguationData":[OD(1.0)],"derivedFrom":[makeQuery(id+"F10.opExtrude","CAP_FACE",FACE,{"disambiguationData":[OSD([sQuery(id+"F2.wireOp",EDGE,"E12"),sQuery(id+"F2.wireOp",EDGE,"E13"),sQuery(id+"F2.wireOp",EDGE,"E14"),sQuery(id+"F2.wireOp",EDGE,"E15"),sQuery(id+"F2.wireOp",EDGE,"E16"),sQuery(id+"F2.wireOp",EDGE,"E17"),sQuery(id+"F2.wireOp",EDGE,"E18"),sQuery(id+"F2.wireOp",EDGE,"E19"),sQuery(id+"F2.wireOp",EDGE,"E20"),sQuery(id+"F2.wireOp",EDGE,"E21")])],"isStart":true}),makeQuery(id+"F12.opExtrude","SWEPT_FACE",FACE,{"disambiguationData":[OSD([sQuery(id+"F11.wireOp",EDGE,"E69")])]})]});
            var Q9;
            Q9=makeQuery(id+"F10.opExtrude","CAP_EDGE",EDGE,{"disambiguationData":[OSD([sQuery(id+"F2.wireOp",EDGE,"E16"),sQuery(id+"F2.wireOp",EDGE,"E19")])],"isStart":true});
            var Q10;
            Q10=makeQuery(id+"F10.opExtrude","CAP_EDGE",EDGE,{"disambiguationData":[OSD([sQuery(id+"F2.wireOp",EDGE,"E18")])],"isStart":true});
            var Q11;
            Q11=makeQuery(id+"F10.opExtrude","SWEPT_EDGE",EDGE,{"disambiguationData":[OSD([sQuery(id+"F2.wireOp",EDGE,"E17"),sQuery(id+"F2.wireOp",EDGE,"E18")])]});
            var Q12;
            Q12=makeQuery(id+"F10.opExtrude","SWEPT_EDGE",EDGE,{"disambiguationData":[OSD([sQuery(id+"F2.wireOp",EDGE,"E16"),sQuery(id+"F2.wireOp",EDGE,"E17")])]});
            var Q13;
            Q13=makeQuery(id+"F10.opExtrude","CAP_EDGE",EDGE,{"disambiguationData":[OSD([sQuery(id+"F2.wireOp",EDGE,"E17")])],"isStart":true});
            fillet(context, id + "F48", {"entities" : qUnion([Q0, Q1, Q2, Q3, Q4, Q5, Q6, Q7, Q8, Q9, Q10, Q11, Q12, Q13]), "radius" : 0.5 * mm, "tangentPropagation" : true, "allowEdgeOverflow" : false});
        }
        {
            var Q0;
            Q0=makeQuery(id+"F38.boolean.opBoolean","COPY",FACE,{"derivedFrom":makeQuery(id+"F38.opExtrude","SWEPT_FACE",FACE,{"disambiguationData":[OSD([sQuery(id+"F37.wireOp",EDGE,"E133.0")])]})});
            var Q1;
            Q1=makeQuery(id+"F38.boolean.opBoolean","COPY",FACE,{"derivedFrom":makeQuery(id+"F38.opExtrude","SWEPT_FACE",FACE,{"disambiguationData":[OSD([sQuery(id+"F37.wireOp",EDGE,"E133.5")])]})});
            var Q2;
            Q2=makeQuery(id+"F38.boolean.opBoolean","COPY",FACE,{"derivedFrom":makeQuery(id+"F38.opExtrude","SWEPT_FACE",FACE,{"disambiguationData":[OSD([sQuery(id+"F37.wireOp",EDGE,"E133.4")])]})});
            var Q3;
            Q3=makeQuery(id+"F38.boolean.opBoolean","COPY",FACE,{"derivedFrom":makeQuery(id+"F38.opExtrude","SWEPT_FACE",FACE,{"disambiguationData":[OSD([sQuery(id+"F37.wireOp",EDGE,"E133.1")])]})});
            var Q4;
            Q4=makeQuery(id+"F38.boolean.opBoolean","COPY",FACE,{"derivedFrom":makeQuery(id+"F38.opExtrude","SWEPT_FACE",FACE,{"disambiguationData":[OSD([sQuery(id+"F37.wireOp",EDGE,"E133.2")])]})});
            var Q5;
            Q5=makeQuery(id+"F38.boolean.opBoolean","COPY",FACE,{"derivedFrom":makeQuery(id+"F38.opExtrude","SWEPT_FACE",FACE,{"disambiguationData":[OSD([sQuery(id+"F37.wireOp",EDGE,"E133.3")])]})});
            fillet(context, id + "F49", {"entities" : qUnion([Q0, Q1, Q2, Q3, Q4, Q5]), "radius" : 0.5 * mm, "tangentPropagation" : true, "allowEdgeOverflow" : false});
        }
        {
            var Q0;
            Q0=makeQuery(id+"F46.boolean.opBoolean","COPY",FACE,{"derivedFrom":makeQuery(id+"F46.opExtrude","SWEPT_FACE",FACE,{"disambiguationData":[OSD([sQuery(id+"F45.wireOp",EDGE,"E142.5")])]})});
            var Q1;
            Q1=makeQuery(id+"F46.boolean.opBoolean","COPY",FACE,{"derivedFrom":makeQuery(id+"F46.opExtrude","SWEPT_FACE",FACE,{"disambiguationData":[OSD([sQuery(id+"F45.wireOp",EDGE,"E142.0")])]})});
            var Q2;
            Q2=makeQuery(id+"F46.boolean.opBoolean","COPY",FACE,{"derivedFrom":makeQuery(id+"F46.opExtrude","SWEPT_FACE",FACE,{"disambiguationData":[OSD([sQuery(id+"F45.wireOp",EDGE,"E142.4")])]})});
            var Q3;
            Q3=makeQuery(id+"F46.boolean.opBoolean","COPY",FACE,{"derivedFrom":makeQuery(id+"F46.opExtrude","SWEPT_FACE",FACE,{"disambiguationData":[OSD([sQuery(id+"F45.wireOp",EDGE,"E142.3")])]})});
            var Q4;
            Q4=makeQuery(id+"F46.boolean.opBoolean","COPY",FACE,{"derivedFrom":makeQuery(id+"F46.opExtrude","SWEPT_FACE",FACE,{"disambiguationData":[OSD([sQuery(id+"F45.wireOp",EDGE,"E142.2")])]})});
            var Q5;
            Q5=makeQuery(id+"F46.boolean.opBoolean","COPY",FACE,{"derivedFrom":makeQuery(id+"F46.opExtrude","SWEPT_FACE",FACE,{"disambiguationData":[OSD([sQuery(id+"F45.wireOp",EDGE,"E142.1")])]})});
            fillet(context, id + "F50", {"entities" : qUnion([Q0, Q1, Q2, Q3, Q4, Q5]), "radius" : 0.5 * mm, "tangentPropagation" : true, "allowEdgeOverflow" : false});
        }
        {
            var Q0;
            Q0=makeQuery(id+"F42.opExtrude","CAP_EDGE",EDGE,{"disambiguationData":[OSD([sQuery(id+"F41.wireOp",EDGE,"E135")])],"isStart":true});
            var Q1;
            Q1=makeQuery(id+"F34.opExtrude","CAP_EDGE",EDGE,{"disambiguationData":[OSD([sQuery(id+"F33.wireOp",EDGE,"E127")])],"isStart":true});
            fillet(context, id + "F51", {"entities" : qUnion([Q0, Q1]), "radius" : 0.5 * mm, "tangentPropagation" : true, "allowEdgeOverflow" : false});
        }
    });
